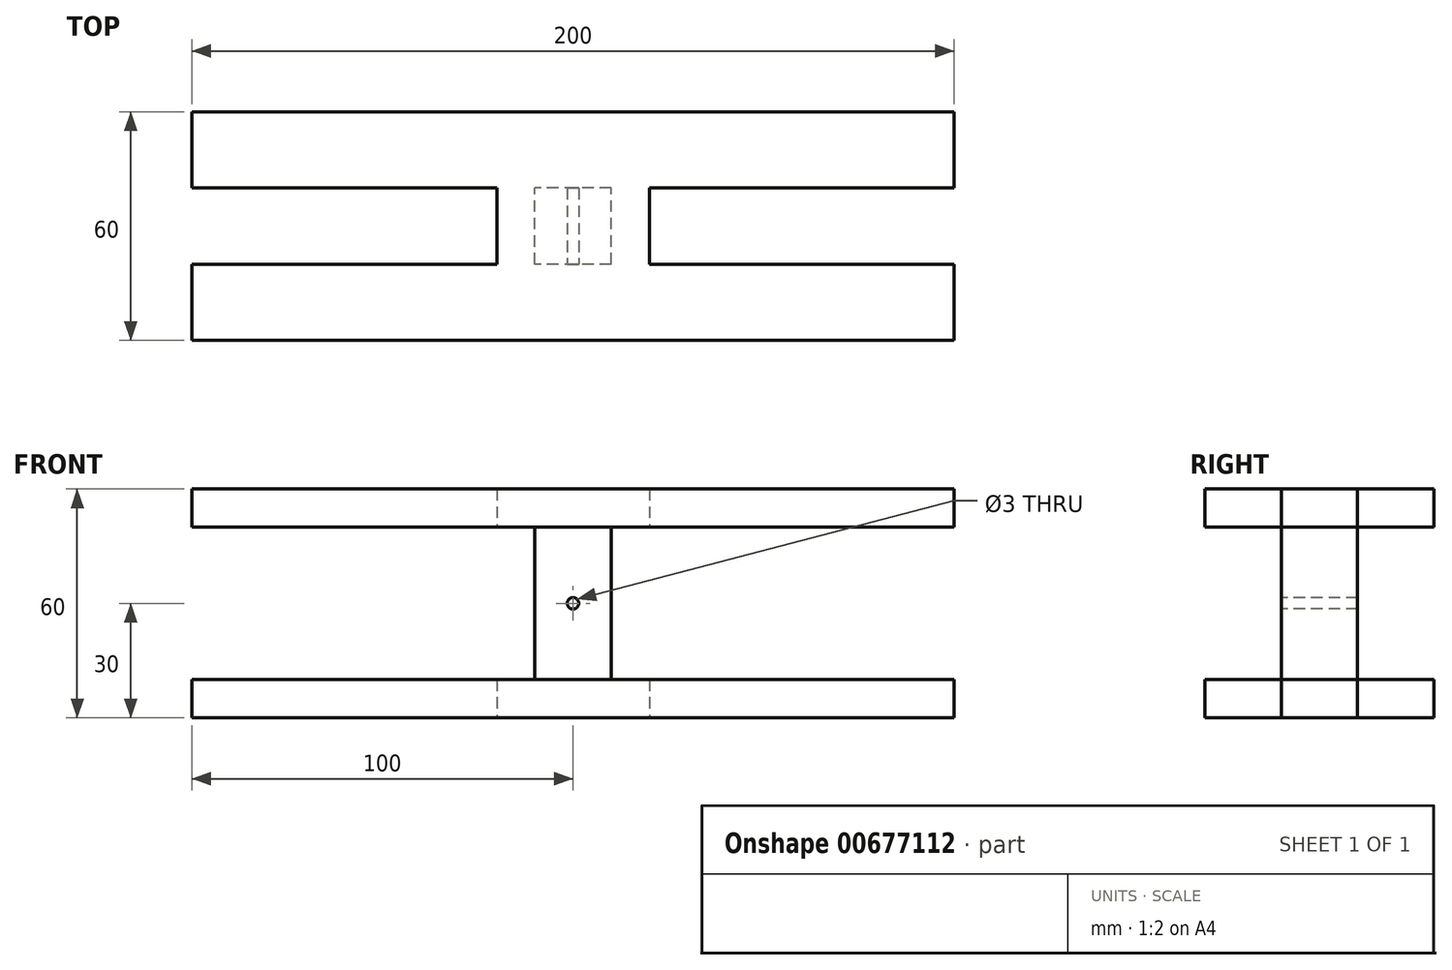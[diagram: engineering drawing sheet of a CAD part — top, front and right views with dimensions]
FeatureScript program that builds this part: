
annotation { "Feature Type Name" : "Feature", "Feature Type Description" : "" }
export const myFeature = defineFeature(function(context is Context, id is Id, definition is map)
    precondition{}
    {
        {
            var Q0;
            Q0=qCreatedBy(makeId("Top.planeOp"),FACE);
            var sketch = newSketch(context, id + "F0", { "sketchPlane" : qUnion([Q0])});
            skLineSegment(sketch, "E0", {"start": v(-100, -30) * mm, "end": v(100, -30) * mm});
            skLineSegment(sketch, "E1", {"start": v(100, -30) * mm, "end": v(100, -10) * mm});
            skLineSegment(sketch, "E2", {"start": v(100, -10) * mm, "end": v(20, -10) * mm});
            skLineSegment(sketch, "E3", {"start": v(20, -10) * mm, "end": v(20, 10) * mm});
            skLineSegment(sketch, "E4", {"start": v(20, 10) * mm, "end": v(100, 10) * mm});
            skLineSegment(sketch, "E5", {"start": v(100, 10) * mm, "end": v(100, 30) * mm});
            skLineSegment(sketch, "E6", {"start": v(100, 30) * mm, "end": v(-100, 30) * mm});
            skLineSegment(sketch, "E7", {"start": v(-100, 30) * mm, "end": v(-100, 10) * mm});
            skLineSegment(sketch, "E8", {"start": v(-100, 10) * mm, "end": v(-20, 10) * mm});
            skLineSegment(sketch, "E9", {"start": v(-20, 10) * mm, "end": v(-20, -10) * mm});
            skLineSegment(sketch, "E10", {"start": v(-20, -10) * mm, "end": v(-100, -10) * mm});
            skLineSegment(sketch, "E11", {"start": v(-100, -10) * mm, "end": v(-100, -30) * mm});
            skSolve(sketch);
        }
        {
            var Q0;
            Q0=makeQuery(id+"F0.imprint","IMPRINT",FACE,{"disambiguationData":[TD([[makeQuery(id+"F0.imprint","IMPRINT",EDGE,{"derivedFrom":sQuery(id+"F0.wireOp",EDGE,"E0")}),1.0]])]});
            extrude(context, id + "F1", {"entities" : qUnion([Q0]), "depth" : 10 * mm, "offsetDistance" : 25 * mm});
        }
        {
            var Q0;
            Q0=makeQuery(id+"F1.opExtrude","CAP_FACE",FACE,{"disambiguationData":[OSD([sQuery(id+"F0.wireOp",EDGE,"E0"),sQuery(id+"F0.wireOp",EDGE,"E1"),sQuery(id+"F0.wireOp",EDGE,"E2"),sQuery(id+"F0.wireOp",EDGE,"E3"),sQuery(id+"F0.wireOp",EDGE,"E4"),sQuery(id+"F0.wireOp",EDGE,"E5"),sQuery(id+"F0.wireOp",EDGE,"E6"),sQuery(id+"F0.wireOp",EDGE,"E7"),sQuery(id+"F0.wireOp",EDGE,"E8"),sQuery(id+"F0.wireOp",EDGE,"E9"),sQuery(id+"F0.wireOp",EDGE,"E10"),sQuery(id+"F0.wireOp",EDGE,"E11")])],"isStart":false});
            var sketch = newSketch(context, id + "F2", { "sketchPlane" : qUnion([Q0])});
            skLineSegment(sketch, "E12.bottom", {"start": v(10, -10) * mm, "end": v(-10, -10) * mm});
            skLineSegment(sketch, "E12.top", {"start": v(10, 10) * mm, "end": v(-10, 10) * mm});
            skLineSegment(sketch, "E12.left", {"start": v(10, -10) * mm, "end": v(10, 10) * mm});
            skLineSegment(sketch, "E12.right", {"start": v(-10, -10) * mm, "end": v(-10, 10) * mm});
            skPoint(sketch, "E12.middle", {"position": v(0, 0) * mm});
            skSolve(sketch);
        }
        {
            var Q0;
            Q0=makeQuery(id+"F2.imprint","IMPRINT",FACE,{"disambiguationData":[TD([[makeQuery(id+"F2.imprint","IMPRINT",EDGE,{"derivedFrom":sQuery(id+"F2.wireOp",EDGE,"E12.bottom")}),-1.0]])]});
            extrude(context, id + "F3", {"entities" : qUnion([Q0]), "operationType" : NewBodyOperationType.ADD, "depth" : 40 * mm, "offsetDistance" : 25 * mm});
        }
        {
            var Q0;
            Q0=makeQuery(id+"F3.opExtrude","SWEPT_FACE",FACE,{"disambiguationData":[OSD([sQuery(id+"F2.wireOp",EDGE,"E12.bottom")])]});
            var sketch = newSketch(context, id + "F4", { "sketchPlane" : qUnion([Q0])});
            skCircle(sketch, "E13", {"center": v(0, 30) * mm, "radius": 1.5 * mm});
            skPoint(sketch, "E13.centerSnap0", {"position": v(-10, 30) * mm});
            skSolve(sketch);
        }
        {
            var Q0;
            Q0=makeQuery(id+"F4.imprint","IMPRINT",FACE,{"disambiguationData":[TD([[makeQuery(id+"F4.imprint","IMPRINT",EDGE,{"derivedFrom":sQuery(id+"F4.wireOp",EDGE,"E13")}),1.0]])]});
            var Q1;
            Q1=sQuery(id+"F4.wireOp",EDGE,"E13");
            extrude(context, id + "F5", {"entities" : qUnion([Q0]), "operationType" : NewBodyOperationType.REMOVE, "surfaceEntities" : qUnion([Q1]), "oppositeDirection" : true, "depth" : 20 * mm, "offsetDistance" : 25 * mm});
        }
        {
            var Q0;
            Q0=makeQuery(id+"F3.opExtrude","CAP_FACE",FACE,{"disambiguationData":[OSD([sQuery(id+"F2.wireOp",EDGE,"E12.bottom"),sQuery(id+"F2.wireOp",EDGE,"E12.top"),sQuery(id+"F2.wireOp",EDGE,"E12.left"),sQuery(id+"F2.wireOp",EDGE,"E12.right")])],"isStart":false});
            var sketch = newSketch(context, id + "F6", { "sketchPlane" : qUnion([Q0])});
            skLineSegment(sketch, "E14.0.0", {"start": v(-20, -10) * mm, "end": v(-100, -10) * mm});
            skLineSegment(sketch, "E14.0.1", {"start": v(-100, -10) * mm, "end": v(-100, -30) * mm});
            skLineSegment(sketch, "E14.0.2", {"start": v(-100, -30) * mm, "end": v(100, -30) * mm});
            skLineSegment(sketch, "E14.0.3", {"start": v(100, -30) * mm, "end": v(100, -10) * mm});
            skLineSegment(sketch, "E14.0.4", {"start": v(100, -10) * mm, "end": v(20, -10) * mm});
            skLineSegment(sketch, "E14.0.5", {"start": v(20, -10) * mm, "end": v(20, 10) * mm});
            skLineSegment(sketch, "E14.0.6", {"start": v(20, 10) * mm, "end": v(100, 10) * mm});
            skLineSegment(sketch, "E14.0.7", {"start": v(100, 10) * mm, "end": v(100, 30) * mm});
            skLineSegment(sketch, "E14.0.8", {"start": v(100, 30) * mm, "end": v(-100, 30) * mm});
            skLineSegment(sketch, "E14.0.9", {"start": v(-100, 30) * mm, "end": v(-100, 10) * mm});
            skLineSegment(sketch, "E14.0.10", {"start": v(-100, 10) * mm, "end": v(-20, 10) * mm});
            skLineSegment(sketch, "E14.0.11", {"start": v(-20, 10) * mm, "end": v(-20, -10) * mm});
            skSolve(sketch);
        }
        {
            var Q0;
            Q0=makeQuery(id+"F6.imprint","IMPRINT",FACE,{"disambiguationData":[TD([[makeQuery(id+"F6.imprint","IMPRINT",EDGE,{"derivedFrom":sQuery(id+"F6.wireOp",EDGE,"E14.0.0")}),1.0]])]});
            var Q1;
            Q1=makeQuery(id+"F6.imprint","IMPRINT",FACE,{"disambiguationData":[TD([[makeQuery(id+"F6.imprint","IMPRINT",EDGE,{"derivedFrom":makeQuery(id+"F3.opExtrude","CAP_EDGE",EDGE,{"disambiguationData":[OSD([sQuery(id+"F2.wireOp",EDGE,"E12.bottom")])],"isStart":false})}),-1.0]])]});
            extrude(context, id + "F7", {"entities" : qUnion([Q0, Q1]), "depth" : 10 * mm, "offsetDistance" : 25 * mm});
        }
    });
